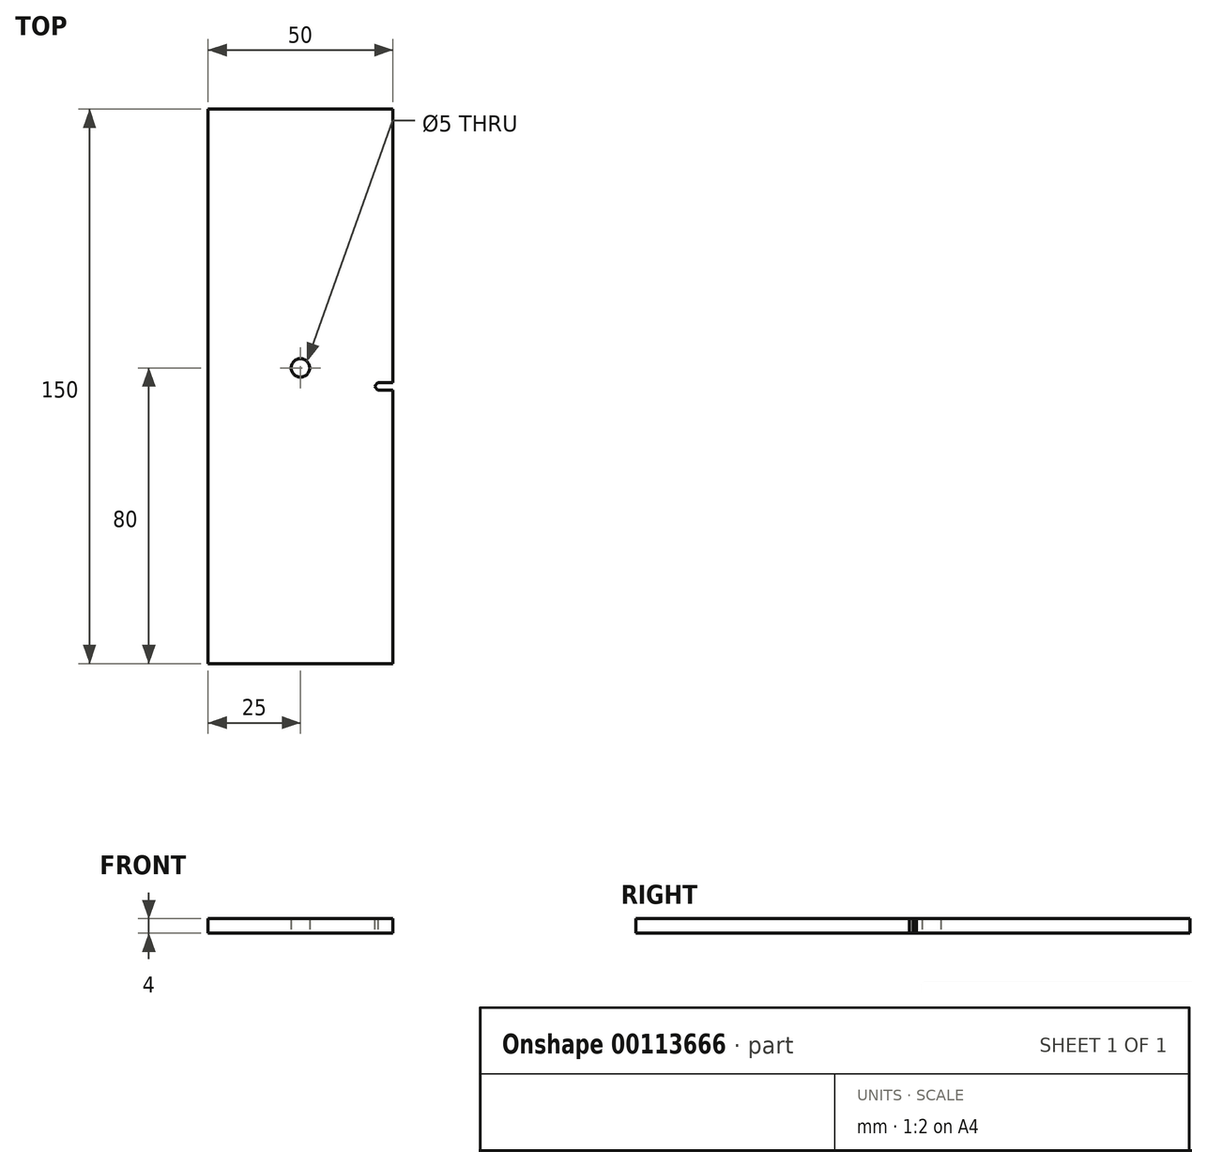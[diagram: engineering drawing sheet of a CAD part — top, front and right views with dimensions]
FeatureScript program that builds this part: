
annotation { "Feature Type Name" : "Feature", "Feature Type Description" : "" }
export const myFeature = defineFeature(function(context is Context, id is Id, definition is map)
    precondition{}
    {
        {
            var Q0;
            Q0=qCreatedBy(makeId("Top.planeOp"),FACE);
            var sketch = newSketch(context, id + "F0", { "sketchPlane" : qUnion([Q0])});
            skLineSegment(sketch, "E0.rect.bottom", {"start": v(25, -75) * mm, "end": v(-25, -75) * mm});
            skLineSegment(sketch, "E0.rect.top", {"start": v(25, 75) * mm, "end": v(-25, 75) * mm});
            skLineSegment(sketch, "E0.rect.left", {"start": v(25, -75) * mm, "end": v(25, 75) * mm});
            skLineSegment(sketch, "E0.rect.right", {"start": v(-25, -75) * mm, "end": v(-25, 75) * mm});
            skPoint(sketch, "E0.rect.middle", {"position": v(0, 0) * mm});
            skPoint(sketch, "E1", {"position": v(25, 1) * mm});
            skLineSegment(sketch, "E2", {"start": v(25, 1) * mm, "end": v(21, 1) * mm});
            skLineSegment(sketch, "E3", {"start": v(21, 1) * mm, "end": v(20, 0) * mm});
            skLineSegment(sketch, "E4.MirrorCS", {"start": v(25, -1) * mm, "end": v(21, -1) * mm});
            skLineSegment(sketch, "E5.MirrorCS", {"start": v(21, -1) * mm, "end": v(20, 0) * mm});
            skPoint(sketch, "E6", {"position": v(0, 5) * mm});
            skCircle(sketch, "E7", {"center": v(0, 5) * mm, "radius": 2.5 * mm});
            skSolve(sketch);
        }
        {
            var Q0;
            {var subQ3=sQuery(id+"F0.wireOp",EDGE,"E0.rect.bottom");Q0=makeQuery(id+"F0.imprint","IMPRINT",FACE,{"disambiguationData":[TD([[makeQuery(id+"F0.imprint","IMPRINT",EDGE,{"derivedFrom":subQ3}),-1.0]])]});}
            extrude(context, id + "F1", {"entities" : qUnion([Q0]), "depth" : 4 * mm});
        }
    });
